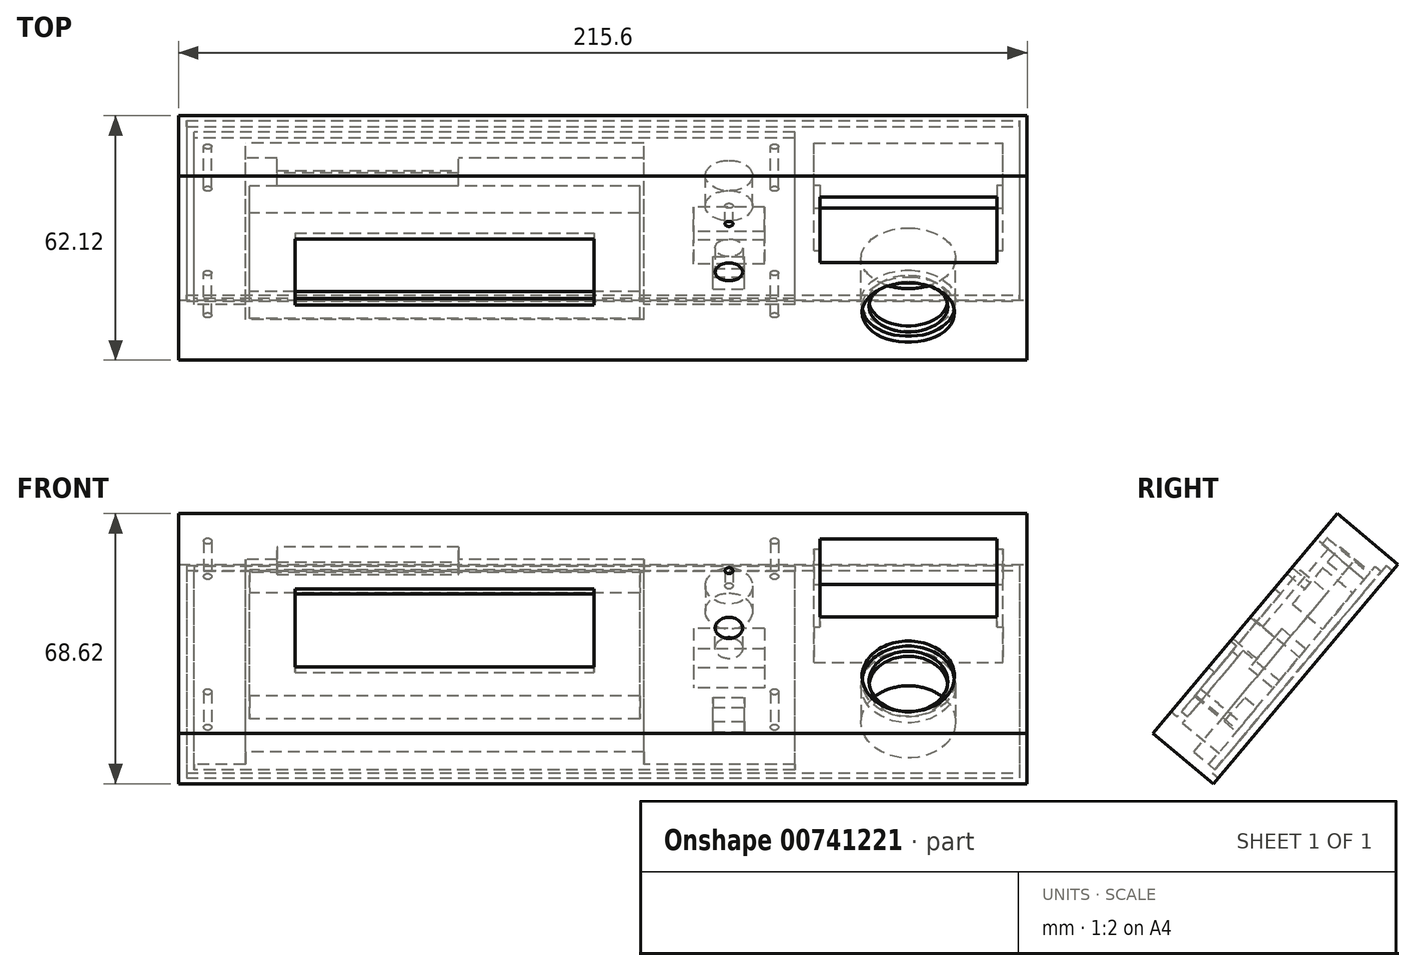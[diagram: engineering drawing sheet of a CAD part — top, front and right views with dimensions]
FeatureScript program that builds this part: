
annotation { "Feature Type Name" : "Feature", "Feature Type Description" : "" }
export const myFeature = defineFeature(function(context is Context, id is Id, definition is map)
    precondition{}
    {
        {
            var Q0;
            Q0=qCreatedBy(makeId("Right.planeOp"),FACE);
            var sketch = newSketch(context, id + "F0", { "sketchPlane" : qUnion([Q0])});
            skLineSegment(sketch, "E0", {"start": v(0, 10) * mm, "end": v(18.47, 32.02) * mm, "construction": true});
            skSolve(sketch);
        }
        {
            var Q0;
            Q0=sQuery(id+"F0.wireOp",EDGE,"E0");
            var Q1;
            Q1=qCreatedBy(makeId("Top.planeOp"),FACE);
            cPlane(context, id + "F1", {"entities" : qUnion([Q0, Q1]), "cplaneType" : CPlaneType.LINE_ANGLE, "offset" : 25 * mm, "angle" : 0 * degree, "width" : 150 * mm, "height" : 150 * mm});
        }
        {
            var Q0;
            Q0=qCreatedBy(id+"F1.planeOp",FACE);
            var sketch = newSketch(context, id + "F2", { "sketchPlane" : qUnion([Q0])});
            skLineSegment(sketch, "E1.bottom", {"start": v(55.16, 42.24) * mm, "end": v(-42.04, 42.24) * mm, "construction": true});
            skLineSegment(sketch, "E1.top", {"start": v(55.16, 2.44) * mm, "end": v(-42.04, 2.44) * mm, "construction": true});
            skLineSegment(sketch, "E1.left", {"start": v(55.16, 42.24) * mm, "end": v(55.16, 2.44) * mm, "construction": true});
            skLineSegment(sketch, "E1.right", {"start": v(-42.04, 42.24) * mm, "end": v(-42.04, 2.44) * mm, "construction": true});
            skLineSegment(sketch, "E2.bottom", {"start": v(44.56, 35.34) * mm, "end": v(-31.44, 35.34) * mm, "construction": true});
            skLineSegment(sketch, "E2.top", {"start": v(44.56, 9.34) * mm, "end": v(-31.44, 9.34) * mm, "construction": true});
            skLineSegment(sketch, "E2.left", {"start": v(44.56, 35.34) * mm, "end": v(44.56, 9.34) * mm, "construction": true});
            skLineSegment(sketch, "E2.right", {"start": v(-31.44, 35.34) * mm, "end": v(-31.44, 9.34) * mm, "construction": true});
            skPoint(sketch, "E2.middle", {"position": v(6.56, 22.34) * mm});
            skPoint(sketch, "E2.middle.positionSnap0", {"position": v(55.16, 22.34) * mm});
            skPoint(sketch, "E2.middle.positionSnap1", {"position": v(6.56, 42.24) * mm});
            skPoint(sketch, "E2.centerSnap0", {"position": v(55.16, 22.34) * mm});
            skPoint(sketch, "E2.centerSnap1", {"position": v(6.56, 42.24) * mm});
            skLineSegment(sketch, "E3", {"start": v(-65.68, 41.34) * mm, "end": v(-65.68, 5.34) * mm, "construction": true});
            skPoint(sketch, "E4", {"position": v(-65.68, 22.34) * mm});
            skPoint(sketch, "E4.positionSnap0", {"position": v(-42.04, 22.34) * mm});
            skCircle(sketch, "E5", {"center": v(-65.68, 41.34) * mm, "radius": 6 * mm, "construction": true});
            skCircle(sketch, "E6", {"center": v(-65.68, 22.34) * mm, "radius": 3.5 * mm, "construction": true});
            skCircle(sketch, "E7", {"center": v(-65.68, 5.34) * mm, "radius": 1.75 * mm, "construction": true});
            skLineSegment(sketch, "E8.bottom", {"start": v(66.76, 52.84) * mm, "end": v(-77.24, 52.84) * mm, "construction": true});
            skLineSegment(sketch, "E8.top", {"start": v(66.76, 2.84) * mm, "end": v(-77.24, 2.84) * mm, "construction": true});
            skLineSegment(sketch, "E8.left", {"start": v(66.76, 52.84) * mm, "end": v(66.76, 2.84) * mm, "construction": true});
            skLineSegment(sketch, "E8.right", {"start": v(-77.24, 52.84) * mm, "end": v(-77.24, 2.84) * mm, "construction": true});
            skSolve(sketch);
        }
        {
            var Q0;
            Q0=qCreatedBy(id+"F1.planeOp",FACE);
            var sketch = newSketch(context, id + "F3", { "sketchPlane" : qUnion([Q0])});
            skLineSegment(sketch, "E9.bottom", {"start": v(74.16, 60.24) * mm, "end": v(-141.44, 60.24) * mm});
            skLineSegment(sketch, "E9.top", {"start": v(74.16, -12.56) * mm, "end": v(-141.44, -12.56) * mm});
            skLineSegment(sketch, "E9.left", {"start": v(74.16, 60.24) * mm, "end": v(74.16, -12.56) * mm});
            skLineSegment(sketch, "E9.right", {"start": v(-141.44, 60.24) * mm, "end": v(-141.44, -12.56) * mm});
            skLineSegment(sketch, "E10.bottom", {"start": v(69.16, 55.24) * mm, "end": v(-81.44, 55.24) * mm, "construction": true});
            skLineSegment(sketch, "E10.top", {"start": v(69.16, -7.56) * mm, "end": v(-81.44, -7.56) * mm, "construction": true});
            skLineSegment(sketch, "E10.left", {"start": v(69.16, 55.24) * mm, "end": v(69.16, -7.56) * mm, "construction": true});
            skLineSegment(sketch, "E10.right", {"start": v(-81.44, 55.24) * mm, "end": v(-81.44, -7.56) * mm, "construction": true});
            skSolve(sketch);
        }
        {
            var Q0;
            Q0 = qSketchRegion(id + "F3", true);
            extrude(context, id + "F4", {"entities" : qUnion([Q0]), "depth" : 20 * mm, "offsetDistance" : 25 * mm});
        }
        {
            var Q0;
            Q0=makeQuery(id+"F4.opExtrude","CAP_FACE",FACE,{"disambiguationData":[OSD([sQuery(id+"F3.wireOp",EDGE,"E9.bottom"),sQuery(id+"F3.wireOp",EDGE,"E9.top"),sQuery(id+"F3.wireOp",EDGE,"E9.left"),sQuery(id+"F3.wireOp",EDGE,"E9.right")])],"isStart":true});
            var sketch = newSketch(context, id + "F5", { "sketchPlane" : qUnion([Q0])});
            skLineSegment(sketch, "E11.0", {"start": v(-44.56, 35.34) * mm, "end": v(31.44, 35.34) * mm});
            skLineSegment(sketch, "E12.0", {"start": v(-44.56, 35.34) * mm, "end": v(-44.56, 9.34) * mm});
            skLineSegment(sketch, "E13.0", {"start": v(-44.56, 9.34) * mm, "end": v(31.44, 9.34) * mm});
            skLineSegment(sketch, "E14.0", {"start": v(31.44, 35.34) * mm, "end": v(31.44, 9.34) * mm});
            skPoint(sketch, "E15.0", {"position": v(65.68, 22.34) * mm});
            skCircle(sketch, "E16.0", {"center": v(65.68, 22.34) * mm, "radius": 3.5 * mm});
            skSolve(sketch);
        }
        {
            var Q0;
            Q0 = qSketchRegion(id + "F5", true);
            extrude(context, id + "F6", {"entities" : qUnion([Q0]), "operationType" : NewBodyOperationType.REMOVE, "endBound" : BoundingType.THROUGH_ALL, "oppositeDirection" : true, "depth" : 25 * mm, "offsetDistance" : 25 * mm});
        }
        {
            var Q0;
            Q0=makeQuery(id+"F4.opExtrude","CAP_FACE",FACE,{"disambiguationData":[OSD([sQuery(id+"F3.wireOp",EDGE,"E9.bottom"),sQuery(id+"F3.wireOp",EDGE,"E9.top"),sQuery(id+"F3.wireOp",EDGE,"E9.left"),sQuery(id+"F3.wireOp",EDGE,"E9.right")])],"isStart":false});
            var sketch = newSketch(context, id + "F7", { "sketchPlane" : qUnion([Q0])});
            skPoint(sketch, "E17.0", {"position": v(-77.24, 52.84) * mm});
            skPoint(sketch, "E18.0", {"position": v(-77.24, 2.84) * mm});
            skPoint(sketch, "E19.0", {"position": v(66.76, 2.84) * mm});
            skPoint(sketch, "E20.0", {"position": v(66.76, 52.84) * mm});
            skCircle(sketch, "E21", {"center": v(-77.24, 52.84) * mm, "radius": 1 * mm});
            skCircle(sketch, "E22", {"center": v(-77.24, 2.84) * mm, "radius": 1 * mm});
            skCircle(sketch, "E23", {"center": v(66.76, 2.84) * mm, "radius": 1 * mm});
            skCircle(sketch, "E24", {"center": v(66.76, 52.84) * mm, "radius": 1 * mm});
            skSolve(sketch);
        }
        {
            var Q0;
            Q0 = qSketchRegion(id + "F7", true);
            var Q1;
            Q1=makeQuery(id+"F4.opExtrude","CAP_FACE",FACE,{"disambiguationData":[OSD([sQuery(id+"F3.wireOp",EDGE,"E9.bottom"),sQuery(id+"F3.wireOp",EDGE,"E9.top"),sQuery(id+"F3.wireOp",EDGE,"E9.left"),sQuery(id+"F3.wireOp",EDGE,"E9.right")])],"isStart":true});
            extrude(context, id + "F8", {"entities" : qUnion([Q0]), "operationType" : NewBodyOperationType.REMOVE, "endBound" : BoundingType.UP_TO_SURFACE, "oppositeDirection" : true, "depth" : 25 * mm, "endBoundEntityFace" : qUnion([Q1]), "hasOffset" : true, "offsetDistance" : 2 * mm});
        }
        {
            var Q0;
            Q0=makeQuery(id+"F4.opExtrude","CAP_FACE",FACE,{"disambiguationData":[OSD([sQuery(id+"F3.wireOp",EDGE,"E9.bottom"),sQuery(id+"F3.wireOp",EDGE,"E9.top"),sQuery(id+"F3.wireOp",EDGE,"E9.left"),sQuery(id+"F3.wireOp",EDGE,"E9.right")])],"isStart":false});
            var sketch = newSketch(context, id + "F9", { "sketchPlane" : qUnion([Q0])});
            skLineSegment(sketch, "E25.0", {"start": v(56.16, 43.24) * mm, "end": v(-43.04, 43.24) * mm});
            skLineSegment(sketch, "E25.1", {"start": v(56.16, 43.24) * mm, "end": v(56.16, 1.44) * mm});
            skLineSegment(sketch, "E25.2", {"start": v(56.16, 1.44) * mm, "end": v(-43.04, 1.44) * mm});
            skLineSegment(sketch, "E25.3", {"start": v(-43.04, 43.24) * mm, "end": v(-43.04, 1.44) * mm});
            skSolve(sketch);
        }
        {
            var Q0;
            Q0 = qSketchRegion(id + "F9", true);
            var Q1;
            Q1=makeQuery(id+"F4.opExtrude","CAP_FACE",FACE,{"disambiguationData":[OSD([sQuery(id+"F3.wireOp",EDGE,"E9.bottom"),sQuery(id+"F3.wireOp",EDGE,"E9.top"),sQuery(id+"F3.wireOp",EDGE,"E9.left"),sQuery(id+"F3.wireOp",EDGE,"E9.right")])],"isStart":true});
            extrude(context, id + "F10", {"entities" : qUnion([Q0]), "operationType" : NewBodyOperationType.REMOVE, "endBound" : BoundingType.UP_TO_SURFACE, "oppositeDirection" : true, "depth" : 25 * mm, "endBoundEntityFace" : qUnion([Q1]), "hasOffset" : true, "offsetDistance" : 2 * mm});
        }
        {
            var Q0;
            Q0=makeQuery(id+"F4.opExtrude","CAP_FACE",FACE,{"disambiguationData":[OSD([sQuery(id+"F3.wireOp",EDGE,"E9.bottom"),sQuery(id+"F3.wireOp",EDGE,"E9.top"),sQuery(id+"F3.wireOp",EDGE,"E9.left"),sQuery(id+"F3.wireOp",EDGE,"E9.right")])],"isStart":false});
            var sketch = newSketch(context, id + "F11", { "sketchPlane" : qUnion([Q0])});
            skCircle(sketch, "E26", {"center": v(-65.68, 41.34) * mm, "radius": 6 * mm});
            skCircle(sketch, "E27", {"center": v(-65.68, 41.34) * mm, "radius": 1 * mm});
            skSolve(sketch);
        }
        {
            var Q0;
            Q0 = qSketchRegion(id + "F11", true);
            var Q1;
            Q1=makeQuery(id+"F11.imprint","IMPRINT",FACE,{"disambiguationData":[TD([[makeQuery(id+"F11.imprint","IMPRINT",EDGE,{"derivedFrom":sQuery(id+"F11.wireOp",EDGE,"E27")}),1.0]])]});
            var Q2;
            Q2=makeQuery(id+"F10.boolean.opBoolean","COPY",FACE,{"derivedFrom":makeQuery(id+"F10.opExtrude","CAP_FACE",FACE,{"disambiguationData":[OSD([sQuery(id+"F9.wireOp",EDGE,"E25.0"),sQuery(id+"F9.wireOp",EDGE,"E25.1"),sQuery(id+"F9.wireOp",EDGE,"E25.2"),sQuery(id+"F9.wireOp",EDGE,"E25.3")])],"isStart":false})});
            extrude(context, id + "F12", {"entities" : qUnion([Q0, Q1]), "operationType" : NewBodyOperationType.REMOVE, "endBound" : BoundingType.UP_TO_SURFACE, "oppositeDirection" : true, "depth" : 25 * mm, "endBoundEntityFace" : qUnion([Q2]), "hasOffset" : true, "offsetDistance" : 4 * mm});
        }
        {
            var Q0;
            Q0=makeQuery(id+"F11.imprint","IMPRINT",FACE,{"disambiguationData":[TD([[makeQuery(id+"F11.imprint","IMPRINT",EDGE,{"derivedFrom":sQuery(id+"F11.wireOp",EDGE,"E27")}),1.0]])]});
            extrude(context, id + "F13", {"entities" : qUnion([Q0]), "operationType" : NewBodyOperationType.REMOVE, "endBound" : BoundingType.THROUGH_ALL, "oppositeDirection" : true, "depth" : 25 * mm, "offsetDistance" : 25 * mm});
        }
        {
            var Q0;
            Q0=makeQuery(id+"F4.opExtrude","CAP_FACE",FACE,{"disambiguationData":[OSD([sQuery(id+"F3.wireOp",EDGE,"E9.bottom"),sQuery(id+"F3.wireOp",EDGE,"E9.top"),sQuery(id+"F3.wireOp",EDGE,"E9.left"),sQuery(id+"F3.wireOp",EDGE,"E9.right")])],"isStart":false});
            var sketch = newSketch(context, id + "F14", { "sketchPlane" : qUnion([Q0])});
            skLineSegment(sketch, "E28.bottom", {"start": v(-56.68, 15.84) * mm, "end": v(-74.68, 15.84) * mm});
            skLineSegment(sketch, "E28.top", {"start": v(-56.68, 28.84) * mm, "end": v(-74.68, 28.84) * mm});
            skLineSegment(sketch, "E28.left", {"start": v(-56.68, 15.84) * mm, "end": v(-56.68, 28.84) * mm});
            skLineSegment(sketch, "E28.right", {"start": v(-74.68, 15.84) * mm, "end": v(-74.68, 28.84) * mm});
            skPoint(sketch, "E28.middle", {"position": v(-65.68, 22.34) * mm});
            skSolve(sketch);
        }
        {
            var Q0;
            Q0 = qSketchRegion(id + "F14", true);
            var Q1;
            Q1=makeQuery(id+"F10.boolean.opBoolean","COPY",FACE,{"derivedFrom":makeQuery(id+"F10.opExtrude","CAP_FACE",FACE,{"disambiguationData":[OSD([sQuery(id+"F9.wireOp",EDGE,"E25.0"),sQuery(id+"F9.wireOp",EDGE,"E25.1"),sQuery(id+"F9.wireOp",EDGE,"E25.2"),sQuery(id+"F9.wireOp",EDGE,"E25.3")])],"isStart":false})});
            extrude(context, id + "F15", {"entities" : qUnion([Q0]), "operationType" : NewBodyOperationType.REMOVE, "endBound" : BoundingType.UP_TO_SURFACE, "oppositeDirection" : true, "depth" : 25 * mm, "endBoundEntityFace" : qUnion([Q1]), "hasOffset" : true, "offsetDistance" : 6 * mm});
        }
        {
            var Q0;
            Q0=makeQuery(id+"F4.opExtrude","CAP_FACE",FACE,{"disambiguationData":[OSD([sQuery(id+"F3.wireOp",EDGE,"E9.bottom"),sQuery(id+"F3.wireOp",EDGE,"E9.top"),sQuery(id+"F3.wireOp",EDGE,"E9.left"),sQuery(id+"F3.wireOp",EDGE,"E9.right")])],"isStart":false});
            var sketch = newSketch(context, id + "F16", { "sketchPlane" : qUnion([Q0])});
            skLineSegment(sketch, "E29.bottom", {"start": v(-69.68, 9.34) * mm, "end": v(-61.68, 9.34) * mm});
            skLineSegment(sketch, "E29.top", {"start": v(-69.68, 1.34) * mm, "end": v(-61.68, 1.34) * mm});
            skLineSegment(sketch, "E29.left", {"start": v(-69.68, 9.34) * mm, "end": v(-69.68, 1.34) * mm});
            skLineSegment(sketch, "E29.right", {"start": v(-61.68, 9.34) * mm, "end": v(-61.68, 1.34) * mm});
            skPoint(sketch, "E29.middle", {"position": v(-65.68, 5.34) * mm});
            skSolve(sketch);
        }
        {
            var Q0;
            Q0 = qSketchRegion(id + "F16", true);
            var Q1;
            Q1=makeQuery(id+"F10.boolean.opBoolean","COPY",FACE,{"derivedFrom":makeQuery(id+"F10.opExtrude","CAP_FACE",FACE,{"disambiguationData":[OSD([sQuery(id+"F9.wireOp",EDGE,"E25.0"),sQuery(id+"F9.wireOp",EDGE,"E25.1"),sQuery(id+"F9.wireOp",EDGE,"E25.2"),sQuery(id+"F9.wireOp",EDGE,"E25.3")])],"isStart":false})});
            extrude(context, id + "F17", {"entities" : qUnion([Q0]), "operationType" : NewBodyOperationType.REMOVE, "endBound" : BoundingType.UP_TO_SURFACE, "oppositeDirection" : true, "depth" : 25 * mm, "endBoundEntityFace" : qUnion([Q1]), "hasOffset" : true, "offsetDistance" : 10 * mm});
        }
        {
            var Q0;
            Q0=makeQuery(id+"F4.opExtrude","CAP_FACE",FACE,{"disambiguationData":[OSD([sQuery(id+"F3.wireOp",EDGE,"E9.bottom"),sQuery(id+"F3.wireOp",EDGE,"E9.top"),sQuery(id+"F3.wireOp",EDGE,"E9.left"),sQuery(id+"F3.wireOp",EDGE,"E9.right")])],"isStart":false});
            var sketch = newSketch(context, id + "F18", { "sketchPlane" : qUnion([Q0])});
            skLineSegment(sketch, "E30.bottom", {"start": v(57.16, 54.24) * mm, "end": v(-44.04, 54.24) * mm});
            skLineSegment(sketch, "E30.top", {"start": v(57.16, -9.56) * mm, "end": v(-44.04, -9.56) * mm});
            skLineSegment(sketch, "E30.left", {"start": v(57.16, 54.24) * mm, "end": v(57.16, -9.56) * mm});
            skLineSegment(sketch, "E30.right", {"start": v(-44.04, 54.24) * mm, "end": v(-44.04, -9.56) * mm});
            skPoint(sketch, "E30.middle", {"position": v(6.56, 22.34) * mm});
            skSolve(sketch);
        }
        {
            var Q0;
            Q0 = qSketchRegion(id + "F18", true);
            var Q1;
            Q1=makeQuery(id+"F10.boolean.opBoolean","COPY",FACE,{"derivedFrom":makeQuery(id+"F10.opExtrude","CAP_FACE",FACE,{"disambiguationData":[OSD([sQuery(id+"F9.wireOp",EDGE,"E25.0"),sQuery(id+"F9.wireOp",EDGE,"E25.1"),sQuery(id+"F9.wireOp",EDGE,"E25.2"),sQuery(id+"F9.wireOp",EDGE,"E25.3")])],"isStart":false})});
            extrude(context, id + "F19", {"entities" : qUnion([Q0]), "operationType" : NewBodyOperationType.REMOVE, "endBound" : BoundingType.UP_TO_SURFACE, "oppositeDirection" : true, "depth" : 25 * mm, "endBoundEntityFace" : qUnion([Q1]), "hasOffset" : true, "offsetDistance" : 9 * mm});
        }
        {
            var Q0;
            Q0=makeQuery(id+"F19.boolean.opBoolean","COPY",FACE,{"derivedFrom":makeQuery(id+"F19.opExtrude","CAP_FACE",FACE,{"disambiguationData":[OSD([sQuery(id+"F18.wireOp",EDGE,"E30.bottom"),sQuery(id+"F18.wireOp",EDGE,"E30.top"),sQuery(id+"F18.wireOp",EDGE,"E30.left"),sQuery(id+"F18.wireOp",EDGE,"E30.right")])],"isStart":false})});
            var sketch = newSketch(context, id + "F20", { "sketchPlane" : qUnion([Q0])});
            skLineSegment(sketch, "E31.bottom", {"start": v(49.16, 49.24) * mm, "end": v(2.96, 49.24) * mm});
            skLineSegment(sketch, "E31.top", {"start": v(49.16, 54.24) * mm, "end": v(2.96, 54.24) * mm});
            skLineSegment(sketch, "E31.left", {"start": v(49.16, 49.24) * mm, "end": v(49.16, 54.24) * mm});
            skLineSegment(sketch, "E31.right", {"start": v(2.96, 49.24) * mm, "end": v(2.96, 54.24) * mm});
            skSolve(sketch);
        }
        {
            var Q0;
            Q0=makeQuery(id+"F20.imprint","IMPRINT",FACE,{"disambiguationData":[TD([[makeQuery(id+"F20.imprint","IMPRINT",EDGE,{"derivedFrom":sQuery(id+"F20.wireOp",EDGE,"E31.bottom")}),-1.0]])]});
            var sketch = newSketch(context, id + "F21", { "sketchPlane" : qUnion([Q0])});
            skSolve(sketch);
        }
        {
            var Q0;
            Q0 = qSketchRegion(id + "F21", true);
            var Q1;
            Q1=makeQuery(id+"F20.imprint","IMPRINT",FACE,{"disambiguationData":[TD([[makeQuery(id+"F20.imprint","IMPRINT",EDGE,{"derivedFrom":sQuery(id+"F20.wireOp",EDGE,"E31.bottom")}),-1.0]])]});
            extrude(context, id + "F22", {"entities" : qUnion([Q0, Q1]), "operationType" : NewBodyOperationType.REMOVE, "oppositeDirection" : true, "depth" : 5 * mm, "offsetDistance" : 25 * mm});
        }
        {
            var Q0;
            Q0=makeQuery(id+"F4.opExtrude","CAP_FACE",FACE,{"disambiguationData":[OSD([sQuery(id+"F3.wireOp",EDGE,"E9.bottom"),sQuery(id+"F3.wireOp",EDGE,"E9.top"),sQuery(id+"F3.wireOp",EDGE,"E9.left"),sQuery(id+"F3.wireOp",EDGE,"E9.right")])],"isStart":false});
            var sketch = newSketch(context, id + "F23", { "sketchPlane" : qUnion([Q0])});
            skLineSegment(sketch, "E32.0", {"start": v(-82.44, 56.24) * mm, "end": v(-82.44, -9.56) * mm});
            skLineSegment(sketch, "E33.0", {"start": v(70.16, 56.24) * mm, "end": v(-82.44, 56.24) * mm});
            skLineSegment(sketch, "E34.0", {"start": v(70.16, 56.24) * mm, "end": v(70.16, -9.56) * mm});
            skLineSegment(sketch, "E35", {"start": v(-82.44, -9.56) * mm, "end": v(70.16, -9.56) * mm});
            skSolve(sketch);
        }
        {
            var Q0;
            Q0 = qSketchRegion(id + "F23", true);
            var Q1;
            Q1=makeQuery(id+"F10.boolean.opBoolean","COPY",FACE,{"derivedFrom":makeQuery(id+"F10.opExtrude","CAP_FACE",FACE,{"disambiguationData":[OSD([sQuery(id+"F9.wireOp",EDGE,"E25.0"),sQuery(id+"F9.wireOp",EDGE,"E25.1"),sQuery(id+"F9.wireOp",EDGE,"E25.2"),sQuery(id+"F9.wireOp",EDGE,"E25.3")])],"isStart":false})});
            extrude(context, id + "F24", {"entities" : qUnion([Q0]), "operationType" : NewBodyOperationType.REMOVE, "endBound" : BoundingType.UP_TO_SURFACE, "oppositeDirection" : true, "depth" : 25 * mm, "endBoundEntityFace" : qUnion([Q1]), "hasOffset" : true, "offsetDistance" : 14 * mm});
        }
        {
            var Q0;
            Q0=makeQuery(id+"F3.imprint","IMPRINT",FACE,{"disambiguationData":[TD([[makeQuery(id+"F3.imprint","IMPRINT",EDGE,{"derivedFrom":sQuery(id+"F3.wireOp",EDGE,"E9.bottom")}),1.0]])]});
            var sketch = newSketch(context, id + "F25", { "sketchPlane" : qUnion([Q0])});
            skLineSegment(sketch, "E36.bottom", {"start": v(-88.75, 51.86) * mm, "end": v(-133.75, 51.86) * mm});
            skLineSegment(sketch, "E36.top", {"start": v(-88.75, 26.06) * mm, "end": v(-133.75, 26.06) * mm});
            skLineSegment(sketch, "E36.left", {"start": v(-88.75, 51.86) * mm, "end": v(-88.75, 26.06) * mm});
            skLineSegment(sketch, "E36.right", {"start": v(-133.75, 51.86) * mm, "end": v(-133.75, 26.06) * mm});
            skLineSegment(sketch, "E37.bottom", {"start": v(-87.25, 53.46) * mm, "end": v(-135.25, 53.46) * mm, "construction": true});
            skLineSegment(sketch, "E37.top", {"start": v(-87.25, 24.46) * mm, "end": v(-135.25, 24.46) * mm, "construction": true});
            skLineSegment(sketch, "E37.left", {"start": v(-87.25, 53.46) * mm, "end": v(-87.25, 24.46) * mm, "construction": true});
            skLineSegment(sketch, "E37.right", {"start": v(-135.25, 53.46) * mm, "end": v(-135.25, 24.46) * mm, "construction": true});
            skPoint(sketch, "E37.middle", {"position": v(-111.25, 38.96) * mm});
            skPoint(sketch, "E37.middle.positionSnap0", {"position": v(-88.75, 38.96) * mm});
            skPoint(sketch, "E37.middle.positionSnap1", {"position": v(-111.25, 26.06) * mm});
            skPoint(sketch, "E37.centerSnap0", {"position": v(-88.75, 38.96) * mm});
            skPoint(sketch, "E37.centerSnap1", {"position": v(-111.25, 26.06) * mm});
            skSolve(sketch);
        }
        {
            var Q0;
            Q0=makeQuery(id+"F25.imprint","IMPRINT",FACE,{"disambiguationData":[TD([[makeQuery(id+"F25.imprint","IMPRINT",EDGE,{"derivedFrom":sQuery(id+"F25.wireOp",EDGE,"E36.bottom")}),1.0]])]});
            extrude(context, id + "F26", {"entities" : qUnion([Q0]), "operationType" : NewBodyOperationType.REMOVE, "endBound" : BoundingType.THROUGH_ALL, "depth" : 25 * mm, "offsetDistance" : 25 * mm});
        }
        {
            var Q0;
            Q0=makeQuery(id+"F4.opExtrude","CAP_FACE",FACE,{"disambiguationData":[OSD([sQuery(id+"F3.wireOp",EDGE,"E9.bottom"),sQuery(id+"F3.wireOp",EDGE,"E9.top"),sQuery(id+"F3.wireOp",EDGE,"E9.left"),sQuery(id+"F3.wireOp",EDGE,"E9.right")])],"isStart":false});
            var sketch = newSketch(context, id + "F27", { "sketchPlane" : qUnion([Q0])});
            skLineSegment(sketch, "E38.bottom", {"start": v(-135.25, 51.86) * mm, "end": v(-87.25, 51.86) * mm});
            skLineSegment(sketch, "E38.top", {"start": v(-135.25, 26.06) * mm, "end": v(-87.25, 26.06) * mm});
            skLineSegment(sketch, "E38.left", {"start": v(-135.25, 51.86) * mm, "end": v(-135.25, 26.06) * mm});
            skLineSegment(sketch, "E38.right", {"start": v(-87.25, 51.86) * mm, "end": v(-87.25, 26.06) * mm});
            skPoint(sketch, "E38.middle", {"position": v(-111.25, 38.96) * mm});
            skPoint(sketch, "E38.middle.positionSnap0", {"position": v(-133.75, 38.96) * mm});
            skPoint(sketch, "E38.middle.positionSnap1", {"position": v(-111.25, 26.06) * mm});
            skPoint(sketch, "E38.centerSnap0", {"position": v(-133.75, 38.96) * mm});
            skPoint(sketch, "E38.centerSnap1", {"position": v(-111.25, 26.06) * mm});
            skSolve(sketch);
        }
        {
            var Q0;
            Q0 = qSketchRegion(id + "F27", true);
            var Q1;
            Q1=makeQuery(id+"F4.opExtrude","CAP_FACE",FACE,{"disambiguationData":[OSD([sQuery(id+"F3.wireOp",EDGE,"E9.bottom"),sQuery(id+"F3.wireOp",EDGE,"E9.top"),sQuery(id+"F3.wireOp",EDGE,"E9.left"),sQuery(id+"F3.wireOp",EDGE,"E9.right")])],"isStart":true});
            extrude(context, id + "F28", {"entities" : qUnion([Q0]), "operationType" : NewBodyOperationType.REMOVE, "endBound" : BoundingType.UP_TO_SURFACE, "oppositeDirection" : true, "depth" : 25 * mm, "endBoundEntityFace" : qUnion([Q1]), "hasOffset" : true, "offsetDistance" : 4 * mm});
        }
        {
            var Q0;
            Q0=makeQuery(id+"F3.imprint","IMPRINT",FACE,{"disambiguationData":[TD([[makeQuery(id+"F3.imprint","IMPRINT",EDGE,{"derivedFrom":sQuery(id+"F3.wireOp",EDGE,"E9.bottom")}),1.0]])]});
            var sketch = newSketch(context, id + "F29", { "sketchPlane" : qUnion([Q0])});
            skLineSegment(sketch, "E39", {"start": v(-111.25, 6.25) * mm, "end": v(-111.25, 38.96) * mm, "construction": true});
            skCircle(sketch, "E40", {"center": v(-111.25, 6.25) * mm, "radius": 10 * mm});
            skCircle(sketch, "E41", {"center": v(-111.25, 6.25) * mm, "radius": 11.75 * mm});
            skSolve(sketch);
        }
        {
            var Q0;
            Q0=makeQuery(id+"F29.imprint","IMPRINT",FACE,{"disambiguationData":[TD([[makeQuery(id+"F29.imprint","IMPRINT",EDGE,{"derivedFrom":sQuery(id+"F29.wireOp",EDGE,"E40")}),1.0]])]});
            extrude(context, id + "F30", {"entities" : qUnion([Q0]), "operationType" : NewBodyOperationType.REMOVE, "endBound" : BoundingType.THROUGH_ALL, "depth" : 25 * mm, "offsetDistance" : 25 * mm});
        }
        {
            var Q0;
            Q0=makeQuery(id+"F29.imprint","IMPRINT",FACE,{"disambiguationData":[TD([[makeQuery(id+"F29.imprint","IMPRINT",EDGE,{"derivedFrom":sQuery(id+"F29.wireOp",EDGE,"E40")}),-1.0]])]});
            extrude(context, id + "F31", {"entities" : qUnion([Q0]), "operationType" : NewBodyOperationType.REMOVE, "depth" : 2 * mm, "offsetDistance" : 25 * mm});
        }
        {
            var Q0;
            Q0=makeQuery(id+"F4.opExtrude","CAP_FACE",FACE,{"disambiguationData":[OSD([sQuery(id+"F3.wireOp",EDGE,"E9.bottom"),sQuery(id+"F3.wireOp",EDGE,"E9.top"),sQuery(id+"F3.wireOp",EDGE,"E9.left"),sQuery(id+"F3.wireOp",EDGE,"E9.right")])],"isStart":false});
            var sketch = newSketch(context, id + "F32", { "sketchPlane" : qUnion([Q0])});
            skCircle(sketch, "E42", {"center": v(-111.25, 6.25) * mm, "radius": 12 * mm});
            skSolve(sketch);
        }
        {
            var Q0;
            Q0 = qSketchRegion(id + "F32", true);
            var Q1;
            Q1=makeQuery(id+"F31.boolean.opBoolean","COPY",FACE,{"derivedFrom":makeQuery(id+"F31.opExtrude","CAP_FACE",FACE,{"disambiguationData":[OSD([sQuery(id+"F29.wireOp",EDGE,"E40"),sQuery(id+"F29.wireOp",EDGE,"E41")])],"isStart":false})});
            extrude(context, id + "F33", {"entities" : qUnion([Q0]), "operationType" : NewBodyOperationType.REMOVE, "endBound" : BoundingType.UP_TO_SURFACE, "oppositeDirection" : true, "depth" : 25 * mm, "endBoundEntityFace" : qUnion([Q1]), "hasOffset" : true, "offsetDistance" : 2 * mm});
        }
        {
            var Q0;
            Q0=makeQuery(id+"F11.imprint","IMPRINT",FACE,{"disambiguationData":[TD([[makeQuery(id+"F11.imprint","IMPRINT",EDGE,{"derivedFrom":sQuery(id+"F11.wireOp",EDGE,"E26")}),-1.0]])]});
            var sketch = newSketch(context, id + "F34", { "sketchPlane" : qUnion([Q0])});
            skLineSegment(sketch, "E43.0", {"start": v(72.16, 58.24) * mm, "end": v(-139.44, 58.24) * mm});
            skLineSegment(sketch, "E43.1", {"start": v(72.16, 58.24) * mm, "end": v(72.16, -10.56) * mm});
            skLineSegment(sketch, "E43.2", {"start": v(72.16, -10.56) * mm, "end": v(-139.44, -10.56) * mm});
            skLineSegment(sketch, "E43.3", {"start": v(-139.44, 58.24) * mm, "end": v(-139.44, -10.56) * mm});
            skSolve(sketch);
        }
        {
            var Q0;
            Q0 = qSketchRegion(id + "F34", true);
            extrude(context, id + "F35", {"entities" : qUnion([Q0]), "operationType" : NewBodyOperationType.REMOVE, "oppositeDirection" : true, "depth" : 2 * mm, "offsetDistance" : 25 * mm});
        }
    });
